# Revit family: ПЗКП-32
name_source: partatom
category: Арматура трубопроводов
units: mm (PartAtom-declared; Revit-internal decimal feet)

## family parameters
Всегда вертикально = Да
На основе рабочей плоскости = Нет
Общий = Нет
При загрузке вырезать с полостями = Нет
Размер круглого соединителя = Использовать диаметр
Тип детали = Клапан - Вставляется

## types (8) — shared parameters
ADSK_Единица измерения = шт.
ADSK_Завод-изготовитель = РУП "БЕЛГАЗТЕХНИКА"
ADSK_Количество = 1
ADSK_Масса_Текст = 18,0 кг
ADSK_Номинальное давление, МПа = 1,2
zero-valued in all types: Отметка по умолчанию

## per-type parameters (varying)
| type | ADSK_Марка | ADSK_Наименование | Левое исполнение | Правое исполнение |
| Л - диапазон настройки 0,0016-0,003 | ПЗКП-32-Л | Клапан ПЗКП-32-Л-(0,0016-0,003) ТУ BY 100270876.171-2013 | Да | Нет |
| Л - диапазон настройки 0,003-0,02 | ПЗКП-32-Л | Клапан ПЗКП-32-Л-(0,003-0,02) ТУ BY 100270876.171-2013 | Да | Нет |
| Л - диапазон настройки 0,02-0,3 | ПЗКП-32-Л | Клапан ПЗКП-32-Л-(0,02-0,3) ТУ BY 100270876.171-2013 | Да | Нет |
| Л - диапазон настройки 0,3-0,6 | ПЗКП-32-Л | Клапан ПЗКП-32-Л-(0,3-0,6) ТУ BY 100270876.171-2013 | Да | Нет |
| П - диапазон настройки 0,0016-0,003 | ПЗКП-32-П | Клапан ПЗКП-32-П-(0,0016-0,003) ТУ BY 100270876.171-2013 | Нет | Да |
| П - диапазон настройки 0,003-0,02 | ПЗКП-32-П | Клапан ПЗКП-32-П-(0,003-0,02) ТУ BY 100270876.171-2013 | Нет | Да |
| П - диапазон настройки 0,02-0,3 | ПЗКП-32-П | Клапан ПЗКП-32-П-(0,02-0,3) ТУ BY 100270876.171-2013 | Нет | Да |
| П - диапазон настройки 0,3-0,6 | ПЗКП-32-П | Клапан ПЗКП-32-П-(0,3-0,6) ТУ BY 100270876.171-2013 | Нет | Да |
